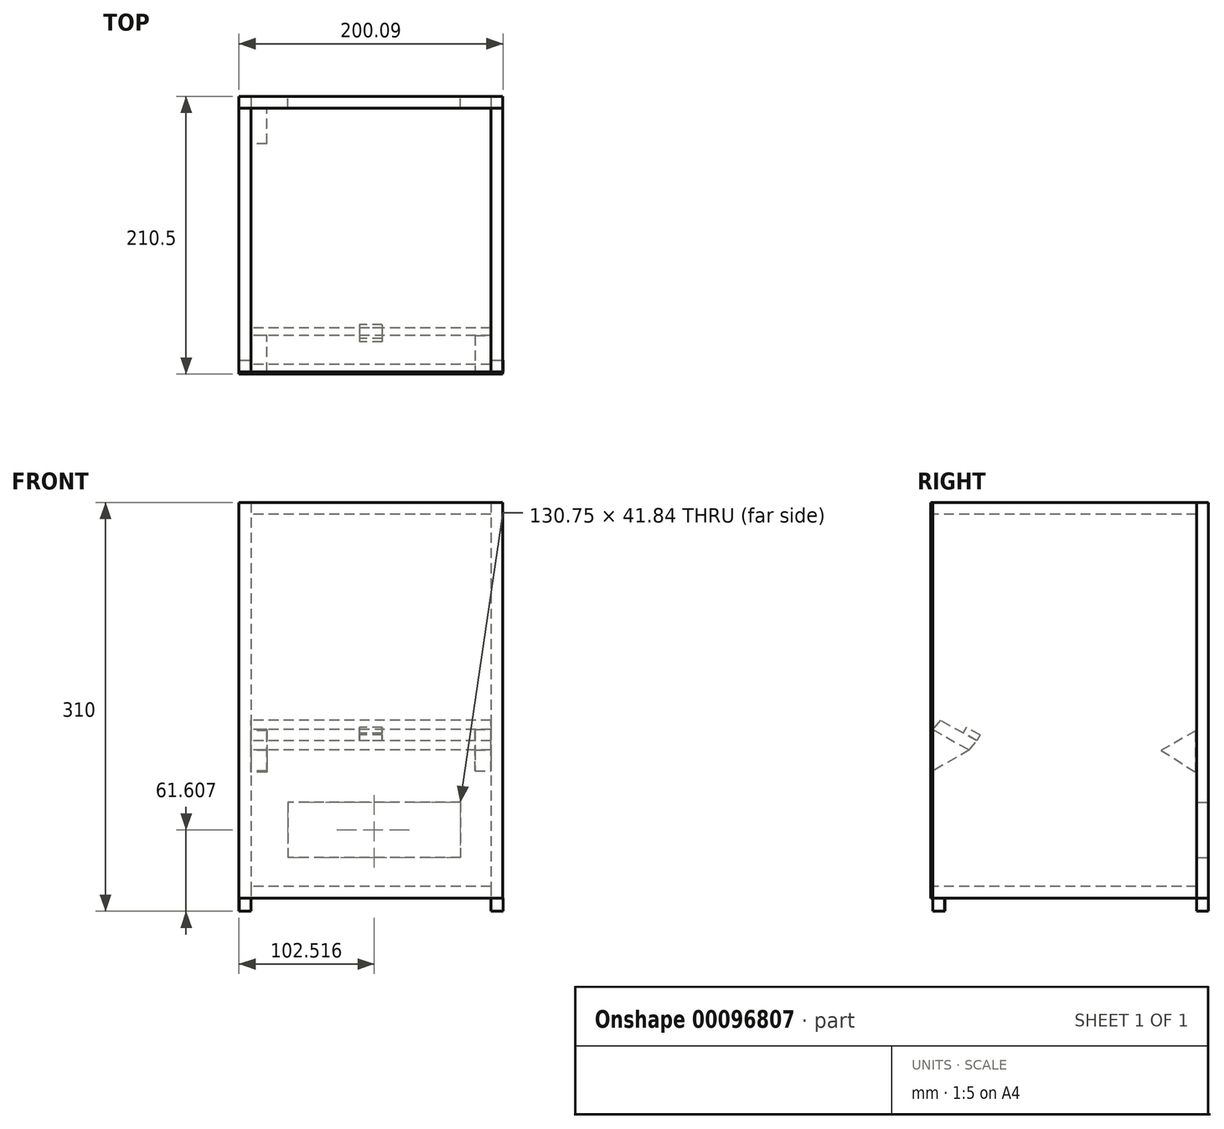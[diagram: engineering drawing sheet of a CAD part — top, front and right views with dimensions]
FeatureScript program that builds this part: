
annotation { "Feature Type Name" : "Feature", "Feature Type Description" : "" }
export const myFeature = defineFeature(function(context is Context, id is Id, definition is map)
    precondition{}
    {
        {
            var Q0;
            Q0=qCreatedBy(makeId("Front.planeOp"),FACE);
            var sketch = newSketch(context, id + "F0", { "sketchPlane" : qUnion([Q0])});
            skLineSegment(sketch, "E0.bottom", {"start": v(0, 0) * mm, "end": v(200, 0) * mm});
            skLineSegment(sketch, "E0.top", {"start": v(0, 300) * mm, "end": v(200, 300) * mm});
            skLineSegment(sketch, "E0.left", {"start": v(0, 0) * mm, "end": v(0, 300) * mm});
            skLineSegment(sketch, "E0.right", {"start": v(200, 0) * mm, "end": v(200, 300) * mm});
            skSolve(sketch);
        }
        {
            var Q0;
            Q0 = qSketchRegion(id + "F0", true);
            extrude(context, id + "F1", {"entities" : qUnion([Q0]), "depth" : 1.5 * mm});
        }
        {
            var Q0;
            Q0=makeQuery(id+"F1.opExtrude","CAP_FACE",FACE,{"disambiguationData":[OSD([sQuery(id+"F0.wireOp",EDGE,"E0.bottom"),sQuery(id+"F0.wireOp",EDGE,"E0.top"),sQuery(id+"F0.wireOp",EDGE,"E0.left"),sQuery(id+"F0.wireOp",EDGE,"E0.right")])],"isStart":true});
            var sketch = newSketch(context, id + "F2", { "sketchPlane" : qUnion([Q0])});
            skLineSegment(sketch, "E1.bottom", {"start": v(0, 300) * mm, "end": v(-9, 300) * mm});
            skLineSegment(sketch, "E1.top", {"start": v(0, 0) * mm, "end": v(-9, 0) * mm});
            skLineSegment(sketch, "E1.left", {"start": v(0, 300) * mm, "end": v(0, 0) * mm});
            skLineSegment(sketch, "E1.right", {"start": v(-9, 300) * mm, "end": v(-9, 0) * mm});
            skSolve(sketch);
        }
        {
            var Q0;
            Q0 = qSketchRegion(id + "F2", true);
            extrude(context, id + "F3", {"entities" : qUnion([Q0]), "depth" : 200 * mm});
        }
        {
            var Q0;
            Q0=makeQuery(id+"F3.opExtrude","SWEPT_FACE",FACE,{"disambiguationData":[OSD([sQuery(id+"F2.wireOp",EDGE,"E1.right")])]});
            var sketch = newSketch(context, id + "F4", { "sketchPlane" : qUnion([Q0])});
            skLineSegment(sketch, "E2", {"start": v(0, 96.36) * mm, "end": v(0, 127.78) * mm});
            skLineSegment(sketch, "E3", {"start": v(0, 127.78) * mm, "end": v(27.68, 112.25) * mm});
            skLineSegment(sketch, "E4", {"start": v(27.68, 112.25) * mm, "end": v(0, 96.36) * mm});
            skLineSegment(sketch, "E5", {"start": v(199.33, 95.42) * mm, "end": v(199.33, 126.84) * mm});
            skLineSegment(sketch, "E6", {"start": v(199.33, 126.84) * mm, "end": v(173.08, 112.13) * mm});
            skLineSegment(sketch, "E7", {"start": v(173.08, 112.13) * mm, "end": v(199.33, 95.42) * mm});
            skSolve(sketch);
        }
        {
            var Q0;
            Q0 = qSketchRegion(id + "F4", true);
            extrude(context, id + "F5", {"entities" : qUnion([Q0]), "depth" : 12 * mm});
        }
        {
            var Q0;
            Q0=makeQuery(id+"F3.opExtrude","SWEPT_FACE",FACE,{"disambiguationData":[OSD([sQuery(id+"F2.wireOp",EDGE,"E1.right")])]});
            var sketch = newSketch(context, id + "F6", { "sketchPlane" : qUnion([Q0])});
            skLineSegment(sketch, "E8", {"start": v(27.68, 112.25) * mm, "end": v(33.36, 119.32) * mm});
            skLineSegment(sketch, "E9", {"start": v(33.36, 119.32) * mm, "end": v(5.69, 134.85) * mm});
            skLineSegment(sketch, "E10", {"start": v(5.69, 134.85) * mm, "end": v(0, 127.78) * mm});
            skLineSegment(sketch, "E11", {"start": v(0, 127.78) * mm, "end": v(27.68, 112.25) * mm});
            skSolve(sketch);
        }
        {
            var Q0;
            Q0 = qSketchRegion(id + "F6", true);
            extrude(context, id + "F7", {"entities" : qUnion([Q0]), "depth" : 182 * mm});
        }
        {
            var Q0;
            Q0=makeQuery(id+"F7.opExtrude","SWEPT_FACE",FACE,{"disambiguationData":[OSD([sQuery(id+"F6.wireOp",EDGE,"E9")])]});
            var sketch = newSketch(context, id + "F8", { "sketchPlane" : qUnion([Q0])});
            skLineSegment(sketch, "E12.bottom", {"start": v(108.6, -29.3) * mm, "end": v(91.43, -29.3) * mm});
            skLineSegment(sketch, "E12.top", {"start": v(108.6, -41.2) * mm, "end": v(91.43, -41.2) * mm});
            skLineSegment(sketch, "E12.left", {"start": v(108.6, -29.3) * mm, "end": v(108.6, -41.2) * mm});
            skLineSegment(sketch, "E12.right", {"start": v(91.43, -29.3) * mm, "end": v(91.43, -41.2) * mm});
            skSolve(sketch);
        }
        {
            var Q0;
            Q0 = qSketchRegion(id + "F8", true);
            extrude(context, id + "F9", {"entities" : qUnion([Q0]), "depth" : 5 * mm});
        }
        {
            var Q0;
            Q0=makeQuery(id+"F7.opExtrude","CAP_FACE",FACE,{"disambiguationData":[OSD([sQuery(id+"F6.wireOp",EDGE,"E8"),sQuery(id+"F6.wireOp",EDGE,"E9"),sQuery(id+"F6.wireOp",EDGE,"E10"),sQuery(id+"F6.wireOp",EDGE,"E11")])],"isStart":false});
            var sketch = newSketch(context, id + "F10", { "sketchPlane" : qUnion([Q0])});
            skLineSegment(sketch, "E13", {"start": v(0, 96.36) * mm, "end": v(0, 127.78) * mm});
            skLineSegment(sketch, "E14", {"start": v(0, 127.78) * mm, "end": v(27.68, 112.25) * mm});
            skLineSegment(sketch, "E15", {"start": v(27.68, 112.25) * mm, "end": v(0, 96.36) * mm});
            skSolve(sketch);
        }
        {
            var Q0;
            Q0 = qSketchRegion(id + "F10", true);
            extrude(context, id + "F11", {"entities" : qUnion([Q0]), "oppositeDirection" : true, "depth" : 12 * mm});
        }
        {
            var Q0;
            Q0=makeQuery(id+"F3.opExtrude","SWEPT_FACE",FACE,{"disambiguationData":[OSD([sQuery(id+"F2.wireOp",EDGE,"E1.right")])]});
            var sketch = newSketch(context, id + "F12", { "sketchPlane" : qUnion([Q0])});
            skLineSegment(sketch, "E16.bottom", {"start": v(200, 300) * mm, "end": v(0, 300) * mm});
            skLineSegment(sketch, "E16.top", {"start": v(200, 291) * mm, "end": v(0, 291) * mm});
            skLineSegment(sketch, "E16.left", {"start": v(200, 300) * mm, "end": v(200, 291) * mm});
            skLineSegment(sketch, "E16.right", {"start": v(0, 300) * mm, "end": v(0, 291) * mm});
            skSolve(sketch);
        }
        {
            var Q0;
            Q0 = qSketchRegion(id + "F12", true);
            extrude(context, id + "F13", {"entities" : qUnion([Q0]), "depth" : 182 * mm});
        }
        {
            var Q0;
            Q0=makeQuery(id+"F3.opExtrude","SWEPT_FACE",FACE,{"disambiguationData":[OSD([sQuery(id+"F2.wireOp",EDGE,"E1.right")])]});
            var sketch = newSketch(context, id + "F14", { "sketchPlane" : qUnion([Q0])});
            skLineSegment(sketch, "E17.bottom", {"start": v(200, 0) * mm, "end": v(0, 0) * mm});
            skLineSegment(sketch, "E17.top", {"start": v(200, 9) * mm, "end": v(0, 9) * mm});
            skLineSegment(sketch, "E17.left", {"start": v(200, 0) * mm, "end": v(200, 9) * mm});
            skLineSegment(sketch, "E17.right", {"start": v(0, 0) * mm, "end": v(0, 9) * mm});
            skSolve(sketch);
        }
        {
            var Q0;
            Q0 = qSketchRegion(id + "F14", true);
            extrude(context, id + "F15", {"entities" : qUnion([Q0]), "depth" : 182 * mm});
        }
        {
            var Q0;
            Q0=makeQuery(id+"F1.opExtrude","CAP_FACE",FACE,{"disambiguationData":[OSD([sQuery(id+"F0.wireOp",EDGE,"E0.bottom"),sQuery(id+"F0.wireOp",EDGE,"E0.top"),sQuery(id+"F0.wireOp",EDGE,"E0.left"),sQuery(id+"F0.wireOp",EDGE,"E0.right")])],"isStart":true});
            var sketch = newSketch(context, id + "F16", { "sketchPlane" : qUnion([Q0])});
            skLineSegment(sketch, "E18.bottom", {"start": v(-200, 300) * mm, "end": v(-191, 300) * mm});
            skLineSegment(sketch, "E18.top", {"start": v(-200, 0) * mm, "end": v(-191, 0) * mm});
            skLineSegment(sketch, "E18.left", {"start": v(-200, 300) * mm, "end": v(-200, 0) * mm});
            skLineSegment(sketch, "E18.right", {"start": v(-191, 300) * mm, "end": v(-191, 0) * mm});
            skSolve(sketch);
        }
        {
            var Q0;
            Q0 = qSketchRegion(id + "F16", true);
            extrude(context, id + "F17", {"entities" : qUnion([Q0]), "depth" : 200 * mm});
        }
        {
            var Q0;
            Q0=makeQuery(id+"F17.opExtrude","CAP_FACE",FACE,{"disambiguationData":[OSD([sQuery(id+"F16.wireOp",EDGE,"E18.bottom"),sQuery(id+"F16.wireOp",EDGE,"E18.top"),sQuery(id+"F16.wireOp",EDGE,"E18.left"),sQuery(id+"F16.wireOp",EDGE,"E18.right")])],"isStart":false});
            var sketch = newSketch(context, id + "F18", { "sketchPlane" : qUnion([Q0])});
            skLineSegment(sketch, "E19.bottom", {"start": v(-200, 300) * mm, "end": v(0, 300) * mm});
            skLineSegment(sketch, "E19.top", {"start": v(-200, 0) * mm, "end": v(0, 0) * mm});
            skLineSegment(sketch, "E19.left", {"start": v(-200, 300) * mm, "end": v(-200, 0) * mm});
            skLineSegment(sketch, "E19.right", {"start": v(0, 300) * mm, "end": v(0, 0) * mm});
            skSolve(sketch);
        }
        {
            var Q0;
            Q0 = qSketchRegion(id + "F18", true);
            extrude(context, id + "F19", {"entities" : qUnion([Q0]), "depth" : 9 * mm});
        }
        {
            var Q0;
            Q0=makeQuery(id+"F19.opExtrude","SWEPT_FACE",FACE,{"disambiguationData":[OSD([sQuery(id+"F18.wireOp",EDGE,"E19.top")])]});
            var sketch = newSketch(context, id + "F20", { "sketchPlane" : qUnion([Q0])});
            skLineSegment(sketch, "E20.bottom", {"start": v(0, -209) * mm, "end": v(9, -209) * mm});
            skLineSegment(sketch, "E20.top", {"start": v(0, -200) * mm, "end": v(9, -200) * mm});
            skLineSegment(sketch, "E20.left", {"start": v(0, -209) * mm, "end": v(0, -200) * mm});
            skLineSegment(sketch, "E20.right", {"start": v(9, -209) * mm, "end": v(9, -200) * mm});
            skLineSegment(sketch, "E21.bottom", {"start": v(191.05, -208.94) * mm, "end": v(200.05, -208.94) * mm});
            skLineSegment(sketch, "E21.top", {"start": v(191.05, -199.94) * mm, "end": v(200.05, -199.94) * mm});
            skLineSegment(sketch, "E21.left", {"start": v(191.05, -208.94) * mm, "end": v(191.05, -199.94) * mm});
            skLineSegment(sketch, "E21.right", {"start": v(200.05, -208.94) * mm, "end": v(200.05, -199.94) * mm});
            skLineSegment(sketch, "E22.bottom", {"start": v(191.09, -8.93) * mm, "end": v(200.09, -8.93) * mm});
            skLineSegment(sketch, "E22.top", {"start": v(191.09, 0.07) * mm, "end": v(200.09, 0.07) * mm});
            skLineSegment(sketch, "E22.left", {"start": v(191.09, -8.93) * mm, "end": v(191.09, 0.07) * mm});
            skLineSegment(sketch, "E22.right", {"start": v(200.09, -8.93) * mm, "end": v(200.09, 0.07) * mm});
            skLineSegment(sketch, "E23.bottom", {"start": v(0.17, -9.07) * mm, "end": v(9.17, -9.07) * mm});
            skLineSegment(sketch, "E23.top", {"start": v(0.17, -0.07) * mm, "end": v(9.17, -0.07) * mm});
            skLineSegment(sketch, "E23.left", {"start": v(0.17, -9.07) * mm, "end": v(0.17, -0.07) * mm});
            skLineSegment(sketch, "E23.right", {"start": v(9.17, -9.07) * mm, "end": v(9.17, -0.07) * mm});
            skSolve(sketch);
        }
        {
            var Q0;
            Q0 = qSketchRegion(id + "F20", true);
            extrude(context, id + "F21", {"entities" : qUnion([Q0]), "depth" : 10 * mm});
        }
        {
            var Q0;
            Q0=makeQuery(id+"F19.opExtrude","CAP_FACE",FACE,{"disambiguationData":[OSD([sQuery(id+"F18.wireOp",EDGE,"E19.bottom"),sQuery(id+"F18.wireOp",EDGE,"E19.top"),sQuery(id+"F18.wireOp",EDGE,"E19.left"),sQuery(id+"F18.wireOp",EDGE,"E19.right")])],"isStart":false});
            var sketch = newSketch(context, id + "F22", { "sketchPlane" : qUnion([Q0])});
            skLineSegment(sketch, "E24.bottom", {"start": v(-167.9, 72.53) * mm, "end": v(-37.14, 72.53) * mm});
            skLineSegment(sketch, "E24.top", {"start": v(-167.9, 30.69) * mm, "end": v(-37.14, 30.69) * mm});
            skLineSegment(sketch, "E24.left", {"start": v(-167.9, 72.53) * mm, "end": v(-167.9, 30.69) * mm});
            skLineSegment(sketch, "E24.right", {"start": v(-37.14, 72.53) * mm, "end": v(-37.14, 30.69) * mm});
            skSolve(sketch);
        }
        {
            var Q0;
            Q0 = qSketchRegion(id + "F22", true);
            extrude(context, id + "F23", {"entities" : qUnion([Q0]), "operationType" : NewBodyOperationType.REMOVE, "oppositeDirection" : true, "depth" : 9 * mm});
        }
    });
